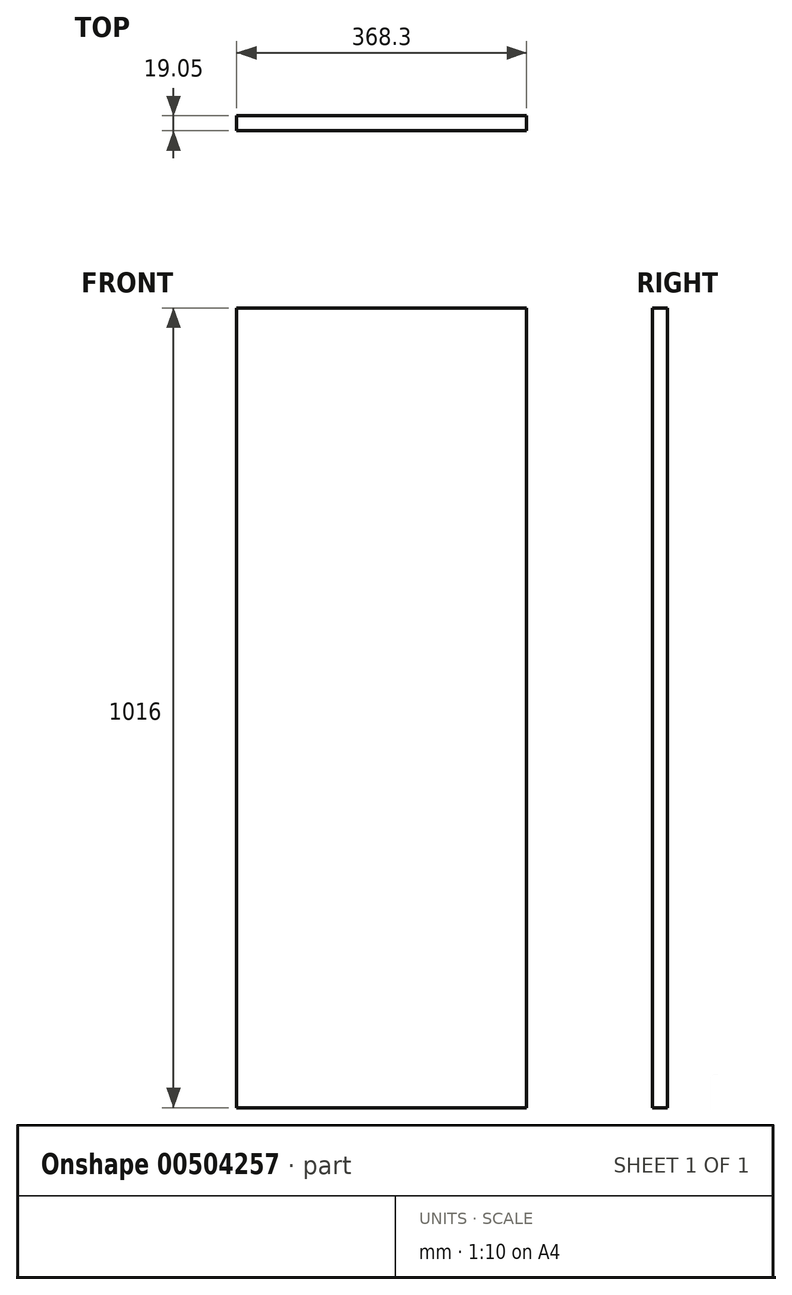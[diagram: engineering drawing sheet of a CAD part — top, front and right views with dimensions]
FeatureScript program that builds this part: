
annotation { "Feature Type Name" : "Feature", "Feature Type Description" : "" }
export const myFeature = defineFeature(function(context is Context, id is Id, definition is map)
    precondition{}
    {
        {
            var Q0;
            Q0=qCreatedBy(makeId("Front.planeOp"),FACE);
            var sketch = newSketch(context, id + "F0", { "sketchPlane" : qUnion([Q0])});
            skLineSegment(sketch, "E0.bottom", {"start": v(184.15, -508) * mm, "end": v(-184.15, -508) * mm});
            skLineSegment(sketch, "E0.top", {"start": v(184.15, 508) * mm, "end": v(-184.15, 508) * mm});
            skLineSegment(sketch, "E0.left", {"start": v(184.15, -508) * mm, "end": v(184.15, 508) * mm});
            skLineSegment(sketch, "E0.right", {"start": v(-184.15, -508) * mm, "end": v(-184.15, 508) * mm});
            skPoint(sketch, "E0.middle", {"position": v(0, 0) * mm});
            skSolve(sketch);
        }
        {
            var Q0;
            Q0=makeQuery(id+"F0.imprint","IMPRINT",FACE,{"disambiguationData":[TD([[makeQuery(id+"F0.imprint","IMPRINT",EDGE,{"derivedFrom":sQuery(id+"F0.wireOp",EDGE,"E0.bottom")}),-1.0]])]});
            extrude(context, id + "F1", {"entities" : qUnion([Q0]), "depth" : 19.05 * mm});
        }
    });
